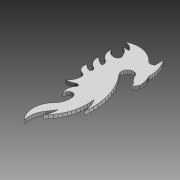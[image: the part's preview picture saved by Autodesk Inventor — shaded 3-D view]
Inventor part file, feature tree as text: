
AUTODESK INVENTOR PART (.ipt)
format: ipt  version: 2018 (Build 220112000, 112)  size: 706,560 bytes
history: native  units: mm
features: other x2, extrude x2, sketch x2
ambient origin geometry x8: Origin, YZ Plane, XZ Plane, XY Plane, X Axis, Y Axis, Z Axis, Center Point
bodies: Body1 (feature_tree)
feature tree (6):
  other  "ソリッド1"
  extrude  "押し出し1"  Depth=2.0mm TaperAngle=0.0deg
  extrude  "押し出し2"  Depth=10.0mm TaperAngle=0.0deg
  sketch  "スケッチ2"
  sketch  "スケッチ3"
  other  "断面エッジを投影1"
